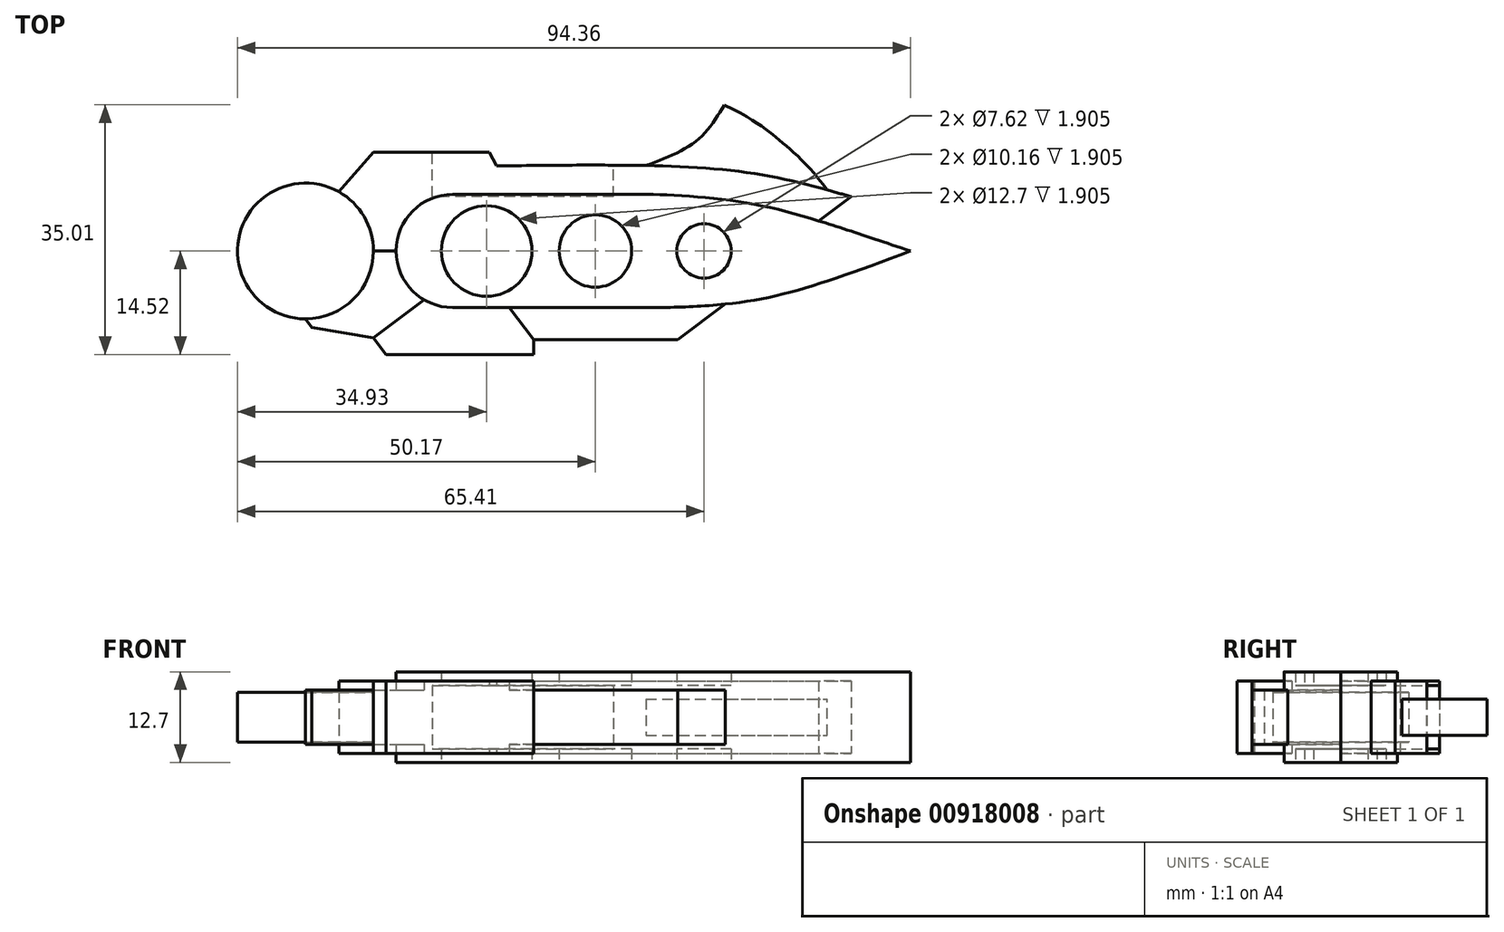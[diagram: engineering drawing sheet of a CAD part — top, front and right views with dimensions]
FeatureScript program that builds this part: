
annotation { "Feature Type Name" : "Feature", "Feature Type Description" : "" }
export const myFeature = defineFeature(function(context is Context, id is Id, definition is map)
    precondition{}
    {
        {
            var Q0;
            Q0=qCreatedBy(makeId("Top.planeOp"),FACE);
            var sketch = newSketch(context, id + "F0", { "sketchPlane" : qUnion([Q0])});
            skCircle(sketch, "E0", {"center": v(0, 0) * mm, "radius": 9.53 * mm});
            skLineSegment(sketch, "E1", {"start": v(9.53, 0) * mm, "end": v(12.7, 0) * mm});
            skArc(sketch, "E2", {"start": v(20.64, 7.94) * mm, "mid": v(12.7, 0) * mm, "end": v(20.64, -7.94) * mm});
            skLineSegment(sketch, "E3", {"start": v(20.64, 7.94) * mm, "end": v(47.02, 7.94) * mm});
            skLineSegment(sketch, "E4", {"start": v(20.64, -7.94) * mm, "end": v(47.02, -7.94) * mm});
            skCircle(sketch, "E5", {"center": v(25.4, 0) * mm, "radius": 6.35 * mm});
            skCircle(sketch, "E6", {"center": v(40.64, 0) * mm, "radius": 5.08 * mm});
            skCircle(sketch, "E7", {"center": v(55.88, 0) * mm, "radius": 3.81 * mm});
            skFitSpline(sketch, "E8", {"points": [v(47.02, 7.94) * mm, v(62.26, 6.67) * mm, v(84.83, 0) * mm], "startDerivative": vector(26.11, 0) * mm, "endDerivative": vector(53.7, -17.7) * mm});
            skFitSpline(sketch, "E9", {"points": [v(47.02, -7.94) * mm, v(61.92, -7.05) * mm, v(84.83, 0) * mm], "startDerivative": vector(26.42, 0) * mm, "endDerivative": vector(53.2, 19.93) * mm});
            skLineSegment(sketch, "E10", {"start": v(4.67, 8.3) * mm, "end": v(9.53, 13.84) * mm});
            skLineSegment(sketch, "E11", {"start": v(9.53, 13.84) * mm, "end": v(25.76, 13.84) * mm});
            skLineSegment(sketch, "E12", {"start": v(25.76, 13.84) * mm, "end": v(28.92, 7.94) * mm});
            skFitSpline(sketch, "E13", {"points": [v(26.79, 11.92) * mm, v(43.33, 12.04) * mm, v(62.26, 10.96) * mm, v(76.47, 7.62) * mm], "startDerivative": vector(48.37, 0.7) * mm, "endDerivative": vector(43.38, -12.38) * mm});
            skLineSegment(sketch, "E14", {"start": v(76.47, 7.62) * mm, "end": v(71.96, 4.23) * mm});
            skLineSegment(sketch, "E15", {"start": v(0, -9.53) * mm, "end": v(0.9, -10.71) * mm});
            skLineSegment(sketch, "E16", {"start": v(0.9, -10.71) * mm, "end": v(9.53, -12.16) * mm});
            skLineSegment(sketch, "E17", {"start": v(9.52, -12.16) * mm, "end": v(16.6, -6.84) * mm});
            skLineSegment(sketch, "E18", {"start": v(9.53, -12.16) * mm, "end": v(11.3, -14.52) * mm});
            skLineSegment(sketch, "E19", {"start": v(11.3, -14.52) * mm, "end": v(31.98, -14.52) * mm});
            skLineSegment(sketch, "E20", {"start": v(31.98, -14.52) * mm, "end": v(31.98, -12.46) * mm});
            skLineSegment(sketch, "E21", {"start": v(31.98, -12.46) * mm, "end": v(28.59, -7.94) * mm});
            skLineSegment(sketch, "E22", {"start": v(31.98, -12.46) * mm, "end": v(52.2, -12.46) * mm});
            skLineSegment(sketch, "E23", {"start": v(52.2, -12.46) * mm, "end": v(58.83, -7.45) * mm});
            skFitSpline(sketch, "E24", {"points": [v(47.72, 11.98) * mm, v(54.68, 15.35) * mm, v(58.75, 20.49) * mm], "startDerivative": vector(14.63, 5.63) * mm, "endDerivative": vector(7.35, 11.72) * mm});
            skFitSpline(sketch, "E25", {"points": [v(58.75, 20.49) * mm, v(66.68, 15.35) * mm, v(73.14, 8.56) * mm], "startDerivative": vector(28.21, -14.1) * mm, "endDerivative": vector(14.35, -20.16) * mm});
            skSolve(sketch);
        }
        {
            var Q0;
            Q0=makeQuery(id+"F0.imprint","IMPRINT",FACE,{"disambiguationData":[TD([[makeQuery(id+"F0.imprint","IMPRINT",EDGE,{"derivedFrom":sQuery(id+"F0.wireOp",EDGE,"E5")}),-1.0]])]});
            extrude(context, id + "F1", {"entities" : qUnion([Q0]), "endBound" : BoundingType.SYMMETRIC, "depth" : 12.7 * mm, "offsetDistance" : 25.4 * mm});
        }
        {
            var Q0;
            {var subQ6=sQuery(id+"F0.wireOp",EDGE,"E1");Q0=makeQuery(id+"F0.imprint","IMPRINT",FACE,{"disambiguationData":[TD([[makeQuery(id+"F0.imprint","IMPRINT",EDGE,{"derivedFrom":subQ6}),1.0]])]});}
            var Q1;
            {var subQ0=sQuery(id+"F0.wireOp",EDGE,"E17");Q1=makeQuery(id+"F0.imprint","IMPRINT",FACE,{"disambiguationData":[TD([[makeQuery(id+"F0.imprint","IMPRINT",EDGE,{"derivedFrom":subQ0}),-1.0]])]});}
            extrude(context, id + "F2", {"entities" : qUnion([Q0, Q1]), "operationType" : NewBodyOperationType.ADD, "endBound" : BoundingType.SYMMETRIC, "depth" : 10.16 * mm, "offsetDistance" : 25.4 * mm});
        }
        {
            var Q0;
            {var subQ2=sQuery(id+"F0.wireOp",EDGE,"E1");Q0=makeQuery(id+"F0.imprint","IMPRINT",FACE,{"disambiguationData":[TD([[makeQuery(id+"F0.imprint","IMPRINT",EDGE,{"derivedFrom":subQ2}),-1.0]])]});}
            var Q1;
            {var subQ0=sQuery(id+"F0.wireOp",EDGE,"E21");Q1=makeQuery(id+"F0.imprint","IMPRINT",FACE,{"disambiguationData":[TD([[makeQuery(id+"F0.imprint","IMPRINT",EDGE,{"derivedFrom":subQ0}),-1.0]])]});}
            extrude(context, id + "F3", {"entities" : qUnion([Q0, Q1]), "operationType" : NewBodyOperationType.ADD, "endBound" : BoundingType.SYMMETRIC, "depth" : 7.62 * mm, "offsetDistance" : 25.4 * mm});
        }
        {
            var Q0;
            {var subQ8=sQuery(id+"F0.wireOp",EDGE,"E14");Q0=makeQuery(id+"F0.imprint","IMPRINT",FACE,{"disambiguationData":[TD([[makeQuery(id+"F0.imprint","IMPRINT",EDGE,{"derivedFrom":subQ8}),-1.0]])]});}
            extrude(context, id + "F4", {"entities" : qUnion([Q0]), "operationType" : NewBodyOperationType.ADD, "endBound" : BoundingType.SYMMETRIC, "depth" : 10.16 * mm, "offsetDistance" : 25.4 * mm});
        }
        {
            var Q0;
            Q0=makeQuery(id+"F0.imprint","IMPRINT",FACE,{"disambiguationData":[TD([[makeQuery(id+"F0.imprint","IMPRINT",EDGE,{"derivedFrom":sQuery(id+"F0.wireOp",EDGE,"E5")}),1.0]])]});
            var Q1;
            Q1=makeQuery(id+"F0.imprint","IMPRINT",FACE,{"disambiguationData":[TD([[makeQuery(id+"F0.imprint","IMPRINT",EDGE,{"derivedFrom":sQuery(id+"F0.wireOp",EDGE,"E6")}),1.0]])]});
            var Q2;
            Q2=makeQuery(id+"F0.imprint","IMPRINT",FACE,{"disambiguationData":[TD([[makeQuery(id+"F0.imprint","IMPRINT",EDGE,{"derivedFrom":sQuery(id+"F0.wireOp",EDGE,"E7")}),1.0]])]});
            extrude(context, id + "F5", {"entities" : qUnion([Q0, Q1, Q2]), "operationType" : NewBodyOperationType.ADD, "endBound" : BoundingType.SYMMETRIC, "depth" : 8.9 * mm, "offsetDistance" : 25.4 * mm});
        }
        {
            var Q0;
            {var subQ0=sQuery(id+"F0.wireOp",EDGE,"E24");Q0=makeQuery(id+"F0.imprint","IMPRINT",FACE,{"disambiguationData":[TD([[makeQuery(id+"F0.imprint","IMPRINT",EDGE,{"derivedFrom":subQ0}),-1.0]])]});}
            extrude(context, id + "F6", {"entities" : qUnion([Q0]), "operationType" : NewBodyOperationType.ADD, "endBound" : BoundingType.SYMMETRIC, "depth" : 5.08 * mm, "offsetDistance" : 25.4 * mm});
        }
        {
            var Q0;
            {var subQ0=sQuery(id+"F0.wireOp",EDGE,"E0");var subQ1=makeQuery(id+"F0.imprint","INTERSECT",VERTEX,{"derivedFrom":[subQ0,sQuery(id+"F0.wireOp",EDGE,"E1")]});Q0=makeQuery(id+"F0.imprint","IMPRINT",FACE,{"disambiguationData":[TD([[makeQuery(id+"F0.imprint","IMPRINT",EDGE,{"disambiguationData":[TD([[subQ1,-1.0]])],"derivedFrom":subQ0}),1.0]])]});}
            extrude(context, id + "F7", {"entities" : qUnion([Q0]), "operationType" : NewBodyOperationType.ADD, "endBound" : BoundingType.SYMMETRIC, "depth" : 7 * mm, "offsetDistance" : 25.4 * mm});
        }
        {
            var Q0;
            Q0=qCreatedBy(makeId("Right.planeOp"),FACE);
            cPlane(context, id + "F8", {"entities" : qUnion([Q0]), "cplaneType" : CPlaneType.OFFSET, "offset" : 17.78 * mm, "width" : 152.4 * mm, "height" : 152.4 * mm});
        }
        {
            var Q0;
            Q0=qCreatedBy(id+"F8.planeOp",FACE);
            var sketch = newSketch(context, id + "F9", { "sketchPlane" : qUnion([Q0])});
            skLineSegment(sketch, "E26.bottom", {"start": v(7.62, 4.45) * mm, "end": v(33.02, 4.45) * mm});
            skLineSegment(sketch, "E26.top", {"start": v(7.62, -4.44) * mm, "end": v(33.02, -4.44) * mm});
            skLineSegment(sketch, "E26.left", {"start": v(7.62, 4.45) * mm, "end": v(7.62, -4.44) * mm});
            skLineSegment(sketch, "E26.right", {"start": v(33.02, 4.45) * mm, "end": v(33.02, -4.44) * mm});
            skPoint(sketch, "E26.middle", {"position": v(20.32, 0) * mm});
            skSolve(sketch);
        }
        {
            var Q0;
            Q0=makeQuery(id+"F9.imprint","IMPRINT",FACE,{"disambiguationData":[TD([[makeQuery(id+"F9.imprint","IMPRINT",EDGE,{"derivedFrom":sQuery(id+"F9.wireOp",EDGE,"E26.bottom")}),-1.0]])]});
            extrude(context, id + "F10", {"entities" : qUnion([Q0]), "operationType" : NewBodyOperationType.REMOVE, "depth" : 25.4 * mm, "offsetDistance" : 25.4 * mm});
        }
    });
